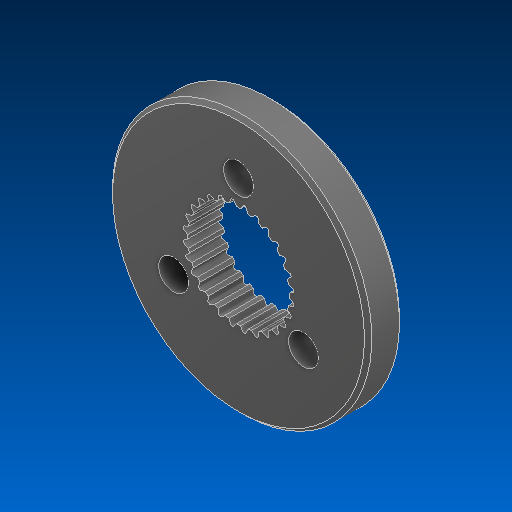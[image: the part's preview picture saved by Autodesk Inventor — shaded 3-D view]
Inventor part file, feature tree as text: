
AUTODESK INVENTOR PART (.ipt)
format: ipt  version: 2022.2 (Build 262287000, 287)  size: 280,576 bytes
history: native  units: in
note: dims shown in document units (in); Inventor stores cm internally (conversion verified against a paired STEP export)
features: chamfer x1
ambient origin geometry x8: Origin, YZ Plane, XZ Plane, XY Plane, X Axis, Y Axis, Z Axis, Center Point
bodies: Solid1 (feature_tree)
feature tree (1):
  chamfer  "Chamfer1"  [1 undecoded]
note: 1 required parameter value undecoded (feature->parameter linkage not recoverable at this tier; creation-order binding heuristic only, values carry confidence <= 0.55)
